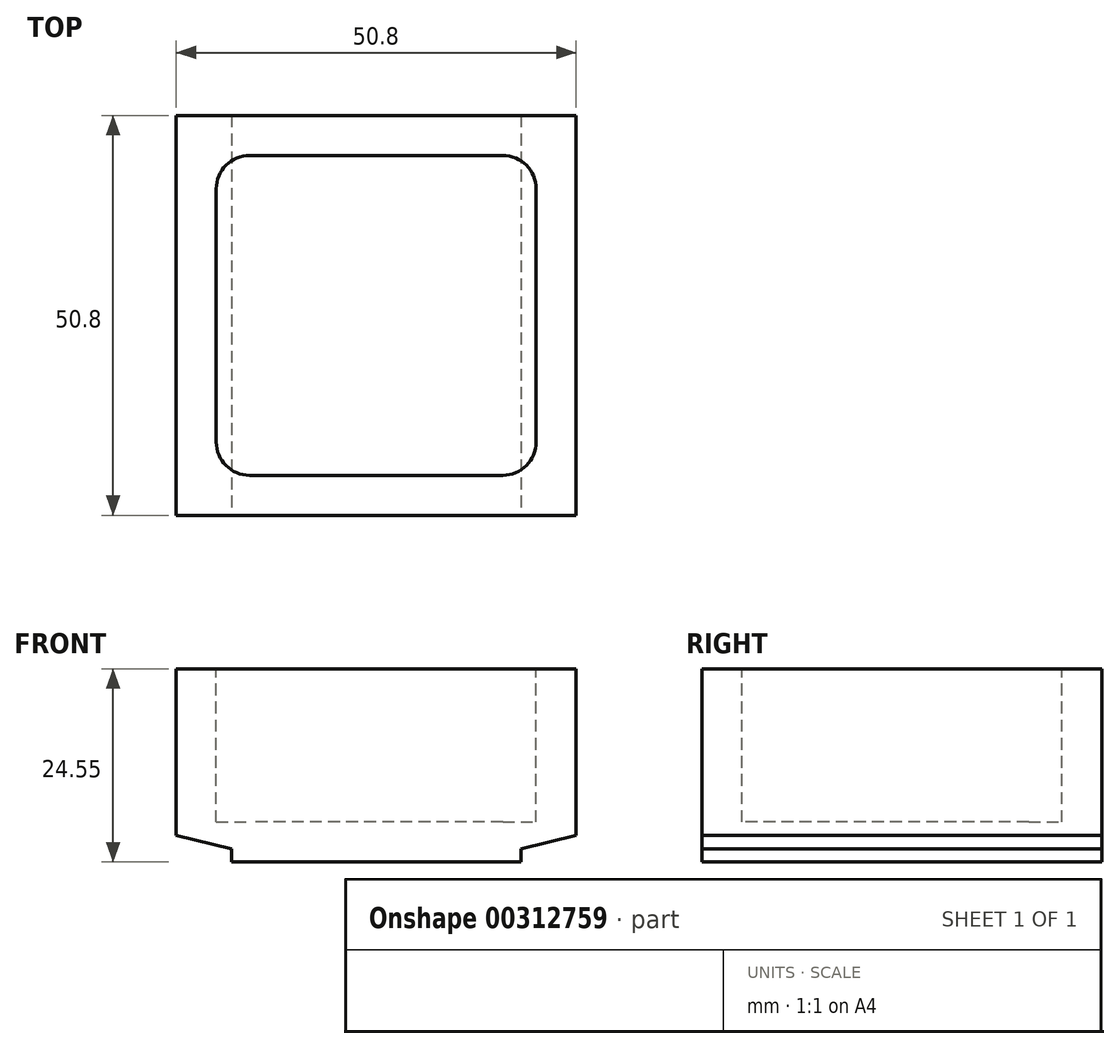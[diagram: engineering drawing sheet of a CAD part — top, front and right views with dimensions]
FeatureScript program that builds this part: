
annotation { "Feature Type Name" : "Feature", "Feature Type Description" : "" }
export const myFeature = defineFeature(function(context is Context, id is Id, definition is map)
    precondition{}
    {
        {
            var Q0;
            Q0=qCreatedBy(makeId("Top.planeOp"),FACE);
            var sketch = newSketch(context, id + "F0", { "sketchPlane" : qUnion([Q0])});
            skLineSegment(sketch, "E0.bottom", {"start": v(38.1, 38.1) * mm, "end": v(-38.1, 38.1) * mm});
            skLineSegment(sketch, "E0.top", {"start": v(38.1, -38.1) * mm, "end": v(-38.1, -38.1) * mm});
            skLineSegment(sketch, "E0.left", {"start": v(38.1, 38.1) * mm, "end": v(38.1, -38.1) * mm});
            skLineSegment(sketch, "E0.right", {"start": v(-38.1, 38.1) * mm, "end": v(-38.1, -38.1) * mm});
            skPoint(sketch, "E0.middle", {"position": v(0, 0) * mm});
            skSolve(sketch);
        }
        {
            var Q0;
            Q0 = qSketchRegion(id + "F0", true);
            extrude(context, id + "F1", {"entities" : qUnion([Q0]), "oppositeDirection" : true, "depth" : 36.83 * mm});
        }
        {
            var Q0;
            Q0=makeQuery(id+"F1.opExtrude","SWEPT_FACE",FACE,{"disambiguationData":[OSD([sQuery(id+"F0.wireOp",EDGE,"E0.top")])]});
            var sketch = newSketch(context, id + "F2", { "sketchPlane" : qUnion([Q0])});
            skLineSegment(sketch, "E1", {"start": v(0, 0) * mm, "end": v(0, -36.83) * mm, "construction": true});
            skLineSegment(sketch, "E2", {"start": v(27.56, -36.83) * mm, "end": v(27.56, -34.3) * mm});
            skLineSegment(sketch, "E3", {"start": v(27.56, -34.3) * mm, "end": v(38.1, -31.75) * mm});
            skLineSegment(sketch, "E4.MirrorCS", {"start": v(-27.56, -36.83) * mm, "end": v(-27.56, -34.3) * mm});
            skLineSegment(sketch, "E5.MirrorCS", {"start": v(-27.56, -34.3) * mm, "end": v(-38.1, -31.75) * mm});
            skSolve(sketch);
        }
        {
            var Q0;
            Q0 = qSketchRegion(id + "F2", true);
            var Q1;
            {var subQ0=sQuery(id+"F2.wireOp",EDGE,"E2");Q1=makeQuery(id+"F2.imprint","IMPRINT",FACE,{"disambiguationData":[TD([[makeQuery(id+"F2.imprint","IMPRINT",EDGE,{"derivedFrom":subQ0}),-1.0]])]});}
            var Q2;
            {var subQ0=sQuery(id+"F2.wireOp",EDGE,"E4.MirrorCS");Q2=makeQuery(id+"F2.imprint","IMPRINT",FACE,{"disambiguationData":[TD([[makeQuery(id+"F2.imprint","IMPRINT",EDGE,{"derivedFrom":subQ0}),1.0]])]});}
            extrude(context, id + "F3", {"entities" : qUnion([Q0, Q1, Q2]), "operationType" : NewBodyOperationType.REMOVE, "endBound" : BoundingType.THROUGH_ALL, "oppositeDirection" : true, "depth" : 25.4 * mm});
        }
        {
            var Q0;
            Q0=makeQuery(id+"F1.opExtrude","CAP_FACE",FACE,{"disambiguationData":[OSD([sQuery(id+"F0.wireOp",EDGE,"E0.bottom"),sQuery(id+"F0.wireOp",EDGE,"E0.top"),sQuery(id+"F0.wireOp",EDGE,"E0.left"),sQuery(id+"F0.wireOp",EDGE,"E0.right")])],"isStart":true});
            var sketch = newSketch(context, id + "F4", { "sketchPlane" : qUnion([Q0])});
            skLineSegment(sketch, "E6.0", {"start": v(24.13, 30.48) * mm, "end": v(-24.13, 30.48) * mm});
            skLineSegment(sketch, "E6.1", {"start": v(30.48, 24.13) * mm, "end": v(30.48, -24.13) * mm});
            skLineSegment(sketch, "E6.2", {"start": v(24.13, -30.48) * mm, "end": v(-24.13, -30.48) * mm});
            skLineSegment(sketch, "E6.3", {"start": v(-30.48, 24.13) * mm, "end": v(-30.48, -24.13) * mm});
            skPoint(sketch, "E7.visualSharp", {"position": v(-30.48, 30.48) * mm});
            skArc(sketch, "E7.filletArc", {"start": v(-24.13, 30.48) * mm, "mid": v(-28.62, 28.62) * mm, "end": v(-30.48, 24.13) * mm});
            skPoint(sketch, "E8.visualSharp", {"position": v(-30.48, -30.48) * mm});
            skArc(sketch, "E8.filletArc", {"start": v(-30.48, -24.13) * mm, "mid": v(-28.62, -28.62) * mm, "end": v(-24.13, -30.48) * mm});
            skPoint(sketch, "E9.visualSharp", {"position": v(30.48, -30.48) * mm});
            skArc(sketch, "E9.filletArc", {"start": v(24.13, -30.48) * mm, "mid": v(28.62, -28.62) * mm, "end": v(30.48, -24.13) * mm});
            skPoint(sketch, "E10.visualSharp", {"position": v(30.48, 30.48) * mm});
            skArc(sketch, "E10.filletArc", {"start": v(30.48, 24.13) * mm, "mid": v(28.62, 28.62) * mm, "end": v(24.13, 30.48) * mm});
            skSolve(sketch);
        }
        {
            var Q0;
            Q0 = qSketchRegion(id + "F4", true);
            extrude(context, id + "F5", {"entities" : qUnion([Q0]), "operationType" : NewBodyOperationType.REMOVE, "oppositeDirection" : true, "depth" : 29.2 * mm});
        }
        {
            var Q0;
            Q0=makeQuery(id+"F1.opExtrude","SWEPT_BODY",BODY,{"disambiguationData":[OSD([sQuery(id+"F0.wireOp",EDGE,"E0.bottom"),sQuery(id+"F0.wireOp",EDGE,"E0.top"),sQuery(id+"F0.wireOp",EDGE,"E0.left"),sQuery(id+"F0.wireOp",EDGE,"E0.right")])]});
            var Q1;
            Q1=qCreatedBy(makeId("Origin.pointOp"),VERTEX);
            transform(context, id + "F6", {"entities" : qUnion([Q0]), "transformType" : TransformType.SCALE_UNIFORMLY, "scale" : .6666, "scalePoint" : qUnion([Q1]), "makeCopy" : false});
        }
    });
